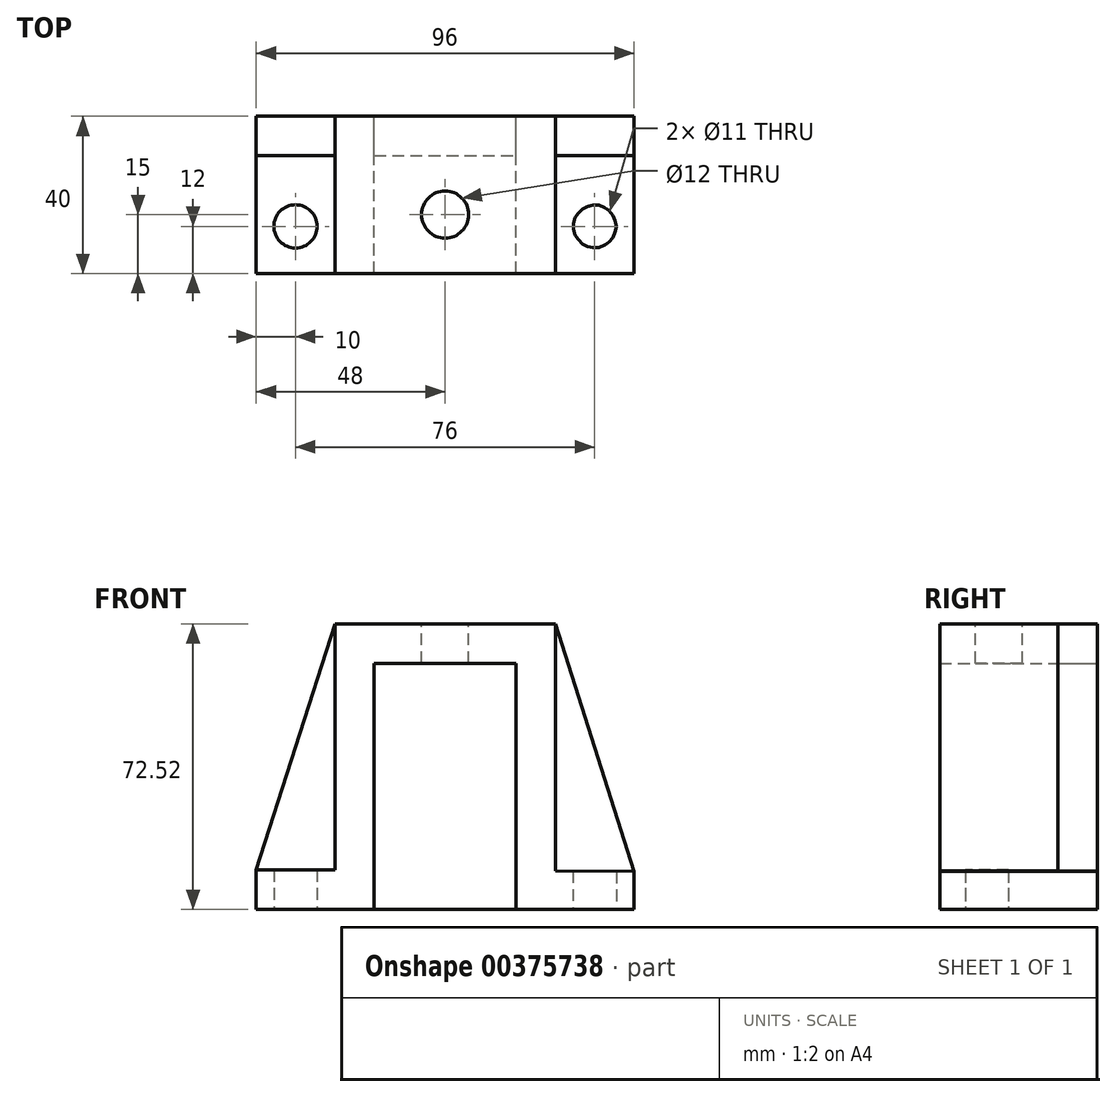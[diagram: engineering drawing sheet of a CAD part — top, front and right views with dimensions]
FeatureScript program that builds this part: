
annotation { "Feature Type Name" : "Feature", "Feature Type Description" : "" }
export const myFeature = defineFeature(function(context is Context, id is Id, definition is map)
    precondition{}
    {
        {
            var Q0;
            Q0=qCreatedBy(makeId("Front.planeOp"),FACE);
            var sketch = newSketch(context, id + "F0", { "sketchPlane" : qUnion([Q0])});
            skLineSegment(sketch, "E0", {"start": v(0, 0) * mm, "end": v(0, 10) * mm});
            skLineSegment(sketch, "E1", {"start": v(0, 10) * mm, "end": v(20, 72.52) * mm});
            skLineSegment(sketch, "E2", {"start": v(30, 0) * mm, "end": v(0, 0) * mm});
            skLineSegment(sketch, "E3.MirrorCS", {"start": v(66, 0) * mm, "end": v(96, 0) * mm});
            skPoint(sketch, "E4.orphan", {"position": v(42.05, 92.46) * mm});
            skLineSegment(sketch, "E5", {"start": v(76, 72.52) * mm, "end": v(76, 9.75) * mm});
            skLineSegment(sketch, "E6", {"start": v(20, 72.52) * mm, "end": v(20, 10) * mm});
            skLineSegment(sketch, "E7", {"start": v(20, 10) * mm, "end": v(0, 10) * mm});
            skLineSegment(sketch, "E8", {"start": v(30, 0) * mm, "end": v(30, 62.52) * mm});
            skLineSegment(sketch, "E9", {"start": v(30, 62.52) * mm, "end": v(66, 62.52) * mm});
            skLineSegment(sketch, "E10", {"start": v(66, 62.52) * mm, "end": v(66, 0) * mm});
            skPoint(sketch, "E11.MirrorCS.start.orphan", {"position": v(101.45, 9.75) * mm});
            skPoint(sketch, "E12.end.orphan", {"position": v(42.05, 72.52) * mm});
            skLineSegment(sketch, "E13", {"start": v(20, 72.52) * mm, "end": v(76, 72.52) * mm});
            skPoint(sketch, "E14.MirrorCS.start.orphan", {"position": v(95, 2.52) * mm});
            skPoint(sketch, "E15.end.orphan", {"position": v(89.55, 10) * mm});
            skLineSegment(sketch, "E16", {"start": v(96, 0) * mm, "end": v(96, 9.6) * mm});
            skLineSegment(sketch, "E17", {"start": v(96, 9.6) * mm, "end": v(76, 9.75) * mm});
            skLineSegment(sketch, "E18", {"start": v(96, 9.6) * mm, "end": v(76, 72.52) * mm});
            skPoint(sketch, "E19.orphan", {"position": v(47.5, 0) * mm});
            skLineSegment(sketch, "E20", {"start": v(30, 0) * mm, "end": v(66, 0) * mm});
            skSolve(sketch);
        }
        {
            var Q0;
            Q0=makeQuery(id+"F0.imprint","IMPRINT",FACE,{"disambiguationData":[TD([[makeQuery(id+"F0.imprint","IMPRINT",EDGE,{"derivedFrom":sQuery(id+"F0.wireOp",EDGE,"E1")}),-1.0]])]});
            var Q1;
            Q1=makeQuery(id+"F0.imprint","IMPRINT",FACE,{"disambiguationData":[TD([[makeQuery(id+"F0.imprint","IMPRINT",EDGE,{"derivedFrom":sQuery(id+"F0.wireOp",EDGE,"E8")}),-1.0]])]});
            var Q2;
            Q2=makeQuery(id+"F0.imprint","IMPRINT",FACE,{"disambiguationData":[TD([[makeQuery(id+"F0.imprint","IMPRINT",EDGE,{"derivedFrom":sQuery(id+"F0.wireOp",EDGE,"E5")}),1.0]])]});
            extrude(context, id + "F1", {"entities" : qUnion([Q0, Q1, Q2]), "depth" : 10 * mm});
        }
        {
            var Q0;
            Q0=makeQuery(id+"F0.imprint","IMPRINT",FACE,{"disambiguationData":[TD([[makeQuery(id+"F0.imprint","IMPRINT",EDGE,{"derivedFrom":sQuery(id+"F0.wireOp",EDGE,"E0")}),-1.0]])]});
            extrude(context, id + "F2", {"entities" : qUnion([Q0]), "depth" : 40 * mm});
        }
        {
            var Q0;
            Q0=qCreatedBy(makeId("Top.planeOp"),FACE);
            var sketch = newSketch(context, id + "F3", { "sketchPlane" : qUnion([Q0])});
            skCircle(sketch, "E21", {"center": v(10, -28) * mm, "radius": 5.5 * mm});
            skCircle(sketch, "E22.MirrorC", {"center": v(86, -28) * mm, "radius": 5.5 * mm});
            skPoint(sketch, "E23.orphan", {"position": v(48, -55.24) * mm});
            skPoint(sketch, "E24.center.orphan", {"position": v(48, -25) * mm});
            skSolve(sketch);
        }
        {
            var Q0;
            Q0 = qSketchRegion(id + "F3", true);
            extrude(context, id + "F4", {"entities" : qUnion([Q0]), "operationType" : NewBodyOperationType.REMOVE, "depth" : 25 * mm});
        }
        {
            var Q0;
            Q0=makeQuery(id+"F2.opExtrude","SWEPT_FACE",FACE,{"disambiguationData":[OSD([sQuery(id+"F0.wireOp",EDGE,"E13")])]});
            var sketch = newSketch(context, id + "F5", { "sketchPlane" : qUnion([Q0])});
            skCircle(sketch, "E25", {"center": v(48, -25) * mm, "radius": 6 * mm});
            skSolve(sketch);
        }
        {
            var Q0;
            Q0=makeQuery(id+"F5.imprint","IMPRINT",FACE,{"disambiguationData":[TD([[makeQuery(id+"F5.imprint","IMPRINT",EDGE,{"derivedFrom":sQuery(id+"F5.wireOp",EDGE,"E25")}),1.0]])]});
            extrude(context, id + "F6", {"entities" : qUnion([Q0]), "operationType" : NewBodyOperationType.REMOVE, "oppositeDirection" : true, "depth" : 25 * mm});
        }
    });
